# Revit family: IS_Multisuite_VV6385_BIM_NL
name_source: partatom
category: Plumbing Fixtures
revit_build: Autodesk Revit MEP 2016 (Build: 20161004_0715(x64)
units: mm (PartAtom-declared; Revit-internal decimal feet)

## family parameters
Always vertical = Yes
Cut with Voids When Loaded = No
OmniClass Number = 23.45.05.21.11
OmniClass Title = Water Closets
Part Type = Normal
Room Calculation Point = No
Round Connector Dimension = Use Diameter
Shared = No
Work Plane-Based = No

## types (1)
- VV638584 - SLIM BEDIENINGSPANEEL CHROOM (AFGEROND)
    Accesoires = www.idealstandardnederland.nl
    Afmetingen = 0
    Afwerking = Chroom
    Artikelnummer = VV638584
    Artikelomschrijving = ISI_ANCILLARY_Wastes_VV638584
    Artikelreferentie = SLIM BEDIENINGSPANEEL CHROOM (AFGEROND)
    Auteur = Ideal Standard
    Barcode = 8028824554860
    Beschrijvinggarantie = 8028824554860
    Breedte = 250
    BrutoGewicht = 0
    Cost = 0 $
    Description = SLIM BEDIENINGSPANEEL CHROOM (AFGEROND)
    Diepte = 360 mm  [stored 1.1811 ft]
    Eigenschappen = Bedieningspaneel afgerond. Chroom.
    Garantieonderdelen = 1
    Garantieunits = Jaar
    Hoogte = 120
    IfcExportAs = Ifc Sanitary Terminal Type
    Installatieinstructies = http://www.idealstandardnederland.nl
    Kleur = Chroom
    Lengte = 360 mm  [stored 1.1811 ft]
    Manufacturer = www.idealstandardnederland.nl
    Materiaal = Messing
    Merk = Ideal Standard
    Model = VV638584
    Nettogewicht = 0
    Revisie = 1
    Telefoonnummer = 31 (0) 77 355 08 08
    Typeconnectie = Sanitair
    URL = www.idealstandardnederland.nl
    Uniclass2015Beschrijving = WC cistern fittings
    Uniclass2015Referentie = Pr_40_20_93_87
    Uniclass2015Version = Products v1.1
    Versie = 1
    Vervangingskosten = 0
    Volumeunits = Liter

note: [stored X ft] marks values corroborated as IEEE doubles in the binary element streams (Revit-internal decimal feet)

## geometry (parser evidence)
native form markers: Blend x4
no freeform markers — native parametric forms only
